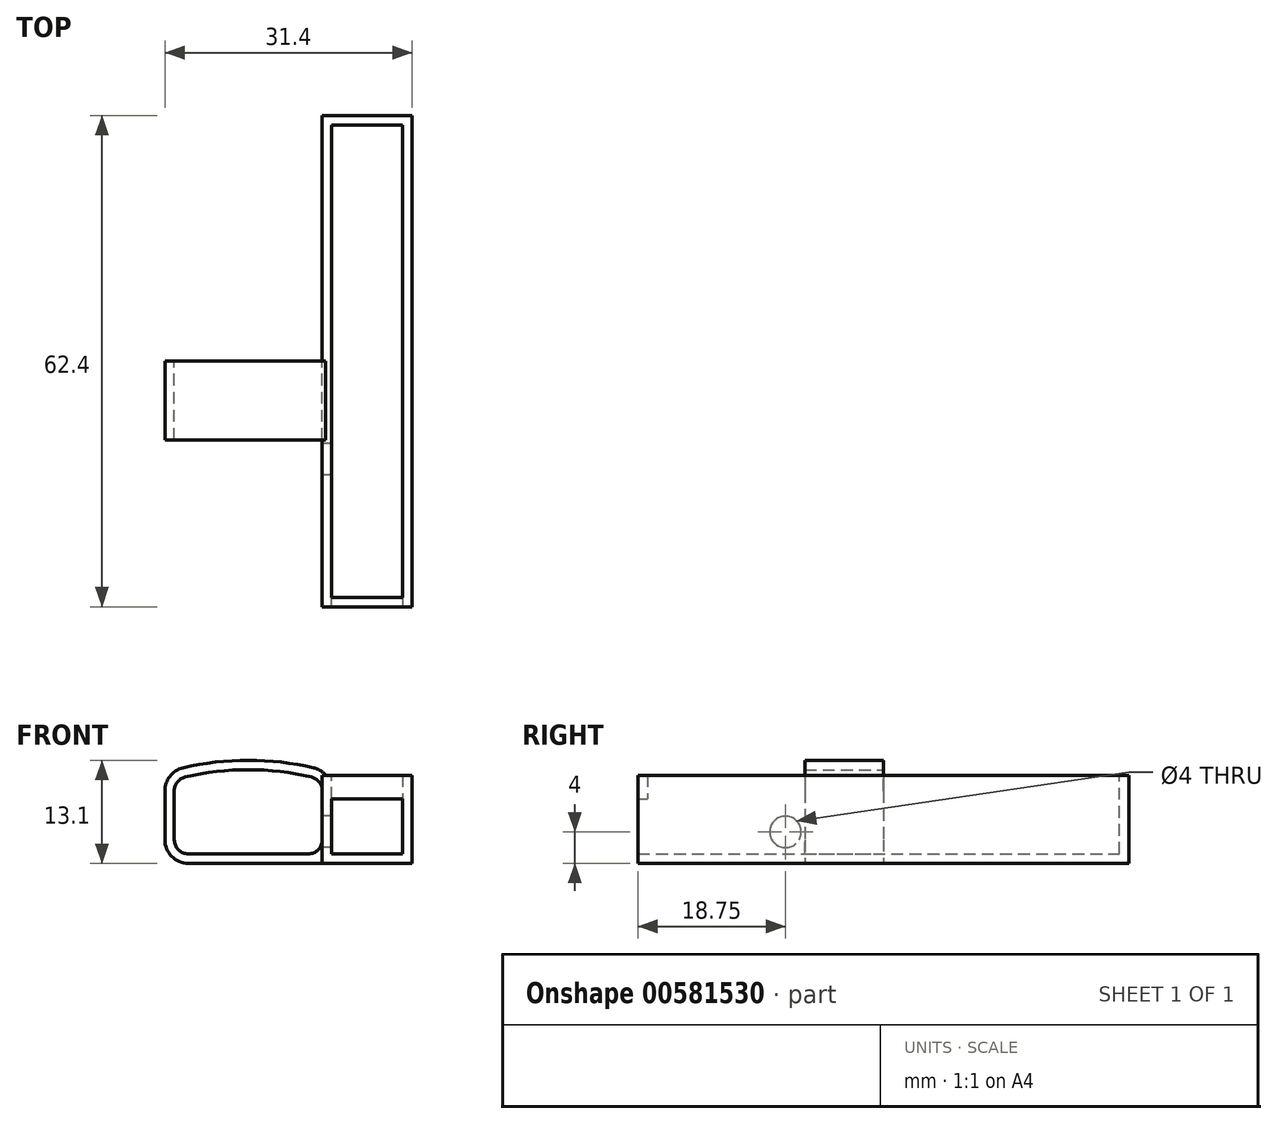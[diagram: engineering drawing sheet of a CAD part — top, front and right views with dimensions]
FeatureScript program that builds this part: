
annotation { "Feature Type Name" : "Feature", "Feature Type Description" : "" }
export const myFeature = defineFeature(function(context is Context, id is Id, definition is map)
    precondition{}
    {
        {
            var Q0;
            Q0=qCreatedBy(makeId("Front.planeOp"),FACE);
            var sketch = newSketch(context, id + "F0", { "sketchPlane" : qUnion([Q0])});
            skLineSegment(sketch, "E0.top", {"start": v(-7.6, -4.7) * mm, "end": v(7.6, -4.7) * mm});
            skLineSegment(sketch, "E0.left", {"start": v(-9.4, 3.3) * mm, "end": v(-9.4, -2.9) * mm});
            skLineSegment(sketch, "E0.right", {"start": v(9.4, 3.3) * mm, "end": v(9.4, -2.9) * mm});
            skPoint(sketch, "E0.middle", {"position": v(0, 0) * mm});
            skArc(sketch, "E1", {"start": v(-8.02, 5.06) * mm, "mid": v(0, 6) * mm, "end": v(8.02, 5.06) * mm});
            skPoint(sketch, "E2", {"position": v(0, 6) * mm});
            skPoint(sketch, "E3", {"position": v(0, -4.7) * mm});
            skPoint(sketch, "E4.visualSharp", {"position": v(-9.4, 4.7) * mm});
            skArc(sketch, "E4.filletArc", {"start": v(-8.02, 5.06) * mm, "mid": v(-9.01, 4.42) * mm, "end": v(-9.4, 3.3) * mm});
            skPoint(sketch, "E5.visualSharp", {"position": v(9.4, 4.7) * mm});
            skArc(sketch, "E5.filletArc", {"start": v(9.4, 3.3) * mm, "mid": v(9.01, 4.42) * mm, "end": v(8.02, 5.06) * mm});
            skPoint(sketch, "E6.visualSharp", {"position": v(-9.4, -4.7) * mm});
            skArc(sketch, "E6.filletArc", {"start": v(-9.4, -2.9) * mm, "mid": v(-8.87, -4.17) * mm, "end": v(-7.6, -4.7) * mm});
            skPoint(sketch, "E7.visualSharp", {"position": v(9.4, -4.7) * mm});
            skArc(sketch, "E7.filletArc", {"start": v(7.6, -4.7) * mm, "mid": v(8.87, -4.17) * mm, "end": v(9.4, -2.9) * mm});
            skSolve(sketch);
        }
        {
            var Q0;
            Q0 = qSketchRegion(id + "F0", true);
            extrude(context, id + "F1", {"entities" : qUnion([Q0]), "depth" : 10 * mm, "offsetDistance" : 25 * mm});
        }
        {
            var Q0;
            Q0=makeQuery(id+"F1.opExtrude","CAP_FACE",FACE,{"disambiguationData":[OSD([sQuery(id+"F0.wireOp",EDGE,"E0.top"),sQuery(id+"F0.wireOp",EDGE,"E0.left"),sQuery(id+"F0.wireOp",EDGE,"E0.right"),sQuery(id+"F0.wireOp",EDGE,"E1"),sQuery(id+"F0.wireOp",EDGE,"E4.filletArc"),sQuery(id+"F0.wireOp",EDGE,"E5.filletArc"),sQuery(id+"F0.wireOp",EDGE,"E6.filletArc"),sQuery(id+"F0.wireOp",EDGE,"E7.filletArc")])],"isStart":true});
            var Q1;
            Q1=makeQuery(id+"F1.opExtrude","CAP_FACE",FACE,{"disambiguationData":[OSD([sQuery(id+"F0.wireOp",EDGE,"E0.top"),sQuery(id+"F0.wireOp",EDGE,"E0.left"),sQuery(id+"F0.wireOp",EDGE,"E0.right"),sQuery(id+"F0.wireOp",EDGE,"E1"),sQuery(id+"F0.wireOp",EDGE,"E4.filletArc"),sQuery(id+"F0.wireOp",EDGE,"E5.filletArc"),sQuery(id+"F0.wireOp",EDGE,"E6.filletArc"),sQuery(id+"F0.wireOp",EDGE,"E7.filletArc")])],"isStart":false});
            shell(context, id + "F2", {"entities" : qUnion([Q0, Q1]), "thickness" : 1.2 * mm, "oppositeDirection" : true});
        }
        {
            var Q0;
            Q0=makeQuery(id+"F1.opExtrude","SWEPT_FACE",FACE,{"disambiguationData":[OSD([sQuery(id+"F0.wireOp",EDGE,"E0.top")])]});
            var sketch = newSketch(context, id + "F3", { "sketchPlane" : qUnion([Q0])});
            skLineSegment(sketch, "E8.bottom", {"start": v(7.6, 10) * mm, "end": v(20.8, 10) * mm});
            skLineSegment(sketch, "E8.top", {"start": v(7.6, 0) * mm, "end": v(20.8, 0) * mm});
            skLineSegment(sketch, "E8.left", {"start": v(7.6, 10) * mm, "end": v(7.6, 0) * mm});
            skLineSegment(sketch, "E8.right", {"start": v(20.8, 10) * mm, "end": v(20.8, 0) * mm});
            skSolve(sketch);
        }
        {
            var Q0;
            Q0=makeQuery(id+"F3.imprint","IMPRINT",FACE,{"disambiguationData":[TD([[makeQuery(id+"F3.imprint","IMPRINT",EDGE,{"derivedFrom":sQuery(id+"F3.wireOp",EDGE,"E8.bottom")}),-1.0]])]});
            var Q1;
            Q1=makeQuery(id+"F2.opShell","OFFSET_FACE",FACE,{"disambiguationData":[OSD([sQuery(id+"F0.wireOp",EDGE,"E0.top")])]});
            extrude(context, id + "F4", {"entities" : qUnion([Q0]), "operationType" : NewBodyOperationType.ADD, "endBound" : BoundingType.UP_TO_SURFACE, "oppositeDirection" : true, "depth" : 25 * mm, "endBoundEntityFace" : qUnion([Q1]), "offsetDistance" : 25 * mm});
        }
        {
            var Q0;
            Q0=makeQuery(id+"F4.opExtrude","CAP_FACE",FACE,{"disambiguationData":[OSD([sQuery(id+"F3.wireOp",EDGE,"E8.bottom"),sQuery(id+"F3.wireOp",EDGE,"E8.top"),sQuery(id+"F3.wireOp",EDGE,"E8.left"),sQuery(id+"F3.wireOp",EDGE,"E8.right")])],"isStart":false});
            var sketch = newSketch(context, id + "F5", { "sketchPlane" : qUnion([Q0])});
            skLineSegment(sketch, "E9.bottom", {"start": v(20.8, 0) * mm, "end": v(19.6, 0) * mm});
            skLineSegment(sketch, "E9.top", {"start": v(20.8, -10) * mm, "end": v(19.6, -10) * mm});
            skLineSegment(sketch, "E9.left", {"start": v(20.8, 0) * mm, "end": v(20.8, -10) * mm});
            skLineSegment(sketch, "E9.right", {"start": v(19.6, 0) * mm, "end": v(19.6, -10) * mm});
            skLineSegment(sketch, "E10.bottom", {"start": v(10.6, -10) * mm, "end": v(10, -10) * mm});
            skLineSegment(sketch, "E10.top", {"start": v(10.6, 0) * mm, "end": v(10, 0) * mm});
            skLineSegment(sketch, "E10.left", {"start": v(10.6, -10) * mm, "end": v(10.6, 0) * mm});
            skLineSegment(sketch, "E10.right", {"start": v(10, -10) * mm, "end": v(10, 0) * mm});
            skSolve(sketch);
        }
        {
            var Q0;
            Q0 = qSketchRegion(id + "F5", true);
            extrude(context, id + "F6", {"entities" : qUnion([Q0]), "operationType" : NewBodyOperationType.ADD, "depth" : 10 * mm, "offsetDistance" : 25 * mm});
        }
        {
            var Q0;
            Q0=qCreatedBy(makeId("Front.planeOp"),FACE);
            var sketch = newSketch(context, id + "F7", { "sketchPlane" : qUnion([Q0])});
            skLineSegment(sketch, "E11.bottom", {"start": v(20.8, 5.3) * mm, "end": v(19.6, 5.3) * mm, "construction": true});
            skLineSegment(sketch, "E11.top", {"start": v(20.8, -5.9) * mm, "end": v(19.6, -5.9) * mm, "construction": true});
            skLineSegment(sketch, "E11.left", {"start": v(20.8, 5.3) * mm, "end": v(20.8, -5.9) * mm, "construction": true});
            skLineSegment(sketch, "E11.right", {"start": v(19.6, 5.3) * mm, "end": v(19.6, -5.9) * mm, "construction": true});
            skLineSegment(sketch, "E12.bottom", {"start": v(20.8, -5.9) * mm, "end": v(10.6, -5.9) * mm, "construction": true});
            skLineSegment(sketch, "E12.top", {"start": v(20.8, -4.7) * mm, "end": v(10.6, -4.7) * mm, "construction": true});
            skLineSegment(sketch, "E12.left", {"start": v(20.8, -5.9) * mm, "end": v(20.8, -4.7) * mm, "construction": true});
            skLineSegment(sketch, "E12.right", {"start": v(10.6, -5.9) * mm, "end": v(10.6, -4.7) * mm, "construction": true});
            skLineSegment(sketch, "E13.bottom", {"start": v(10.6, -5.9) * mm, "end": v(9.4, -5.9) * mm, "construction": true});
            skLineSegment(sketch, "E13.top", {"start": v(10.6, 5.3) * mm, "end": v(9.4, 5.3) * mm, "construction": true});
            skLineSegment(sketch, "E13.left", {"start": v(10.6, -5.9) * mm, "end": v(10.6, 5.3) * mm, "construction": true});
            skLineSegment(sketch, "E14", {"start": v(20.8, 5.3) * mm, "end": v(19.6, 5.3) * mm});
            skLineSegment(sketch, "E15", {"start": v(19.6, 5.3) * mm, "end": v(19.6, -4.7) * mm});
            skLineSegment(sketch, "E16", {"start": v(19.6, -4.7) * mm, "end": v(10.6, -4.7) * mm});
            skLineSegment(sketch, "E17", {"start": v(10.6, 5.3) * mm, "end": v(9.4, 5.3) * mm});
            skLineSegment(sketch, "E18", {"start": v(9.4, -5.9) * mm, "end": v(20.8, -5.9) * mm});
            skLineSegment(sketch, "E19", {"start": v(20.8, 5.3) * mm, "end": v(20.8, -5.9) * mm});
            skLineSegment(sketch, "E20", {"start": v(10.6, 5.3) * mm, "end": v(10.6, -4.7) * mm});
            skLineSegment(sketch, "E21", {"start": v(9.4, -5.9) * mm, "end": v(9.4, 5.3) * mm});
            skSolve(sketch);
        }
        {
            var Q0;
            Q0 = qSketchRegion(id + "F7", true);
            extrude(context, id + "F8", {"entities" : qUnion([Q0]), "operationType" : NewBodyOperationType.ADD, "depth" : 31.2 * mm, "offsetDistance" : 25 * mm, "hasSecondDirection" : true, "secondDirectionOppositeDirection" : true, "secondDirectionDepth" : 31.2 * mm});
        }
        {
            var Q0;
            Q0=makeQuery(id+"F8.boolean.opBoolean","MERGE",FACE,{"derivedFrom":[makeQuery(id+"F2.opShell","OFFSET_FACE",FACE,{"disambiguationData":[OSD([sQuery(id+"F0.wireOp",EDGE,"E0.right")])]}),makeQuery(id+"F8.opExtrude","SWEPT_FACE",FACE,{"disambiguationData":[OSD([sQuery(id+"F7.wireOp",EDGE,"E21")])]})]});
            var sketch = newSketch(context, id + "F9", { "sketchPlane" : qUnion([Q0])});
            skPoint(sketch, "E22", {"position": v(12.45, -1.9) * mm});
            skSolve(sketch);
        }
        {
            var Q0;
            Q0=sQuery(id+"F9.wireOp",VERTEX,"E22");
            var Q1;
            Q1=makeQuery(id+"F1.opExtrude","SWEPT_BODY",BODY,{"disambiguationData":[OSD([sQuery(id+"F0.wireOp",EDGE,"E0.top"),sQuery(id+"F0.wireOp",EDGE,"E0.left"),sQuery(id+"F0.wireOp",EDGE,"E0.right"),sQuery(id+"F0.wireOp",EDGE,"E1"),sQuery(id+"F0.wireOp",EDGE,"E4.filletArc"),sQuery(id+"F0.wireOp",EDGE,"E5.filletArc"),sQuery(id+"F0.wireOp",EDGE,"E6.filletArc"),sQuery(id+"F0.wireOp",EDGE,"E7.filletArc")])]});
            hole(context, id + "F10", {"style" : HoleStyle.SIMPLE, "endStyle" : HoleEndStyle.BLIND, "holeDiameter" : 4 * mm, "majorDiameter" : 5 * mm, "holeDepth" : 5 * mm, "isTappedThrough" : true, "tappedDepth" : 12 * mm, "tapClearance" : 3, "locations" : qUnion([Q0]), "scope" : qUnion([Q1])});
        }
        {
            var Q0;
            Q0=makeQuery(id+"F8.opExtrude","CAP_FACE",FACE,{"disambiguationData":[OSD([sQuery(id+"F7.wireOp",EDGE,"E14"),sQuery(id+"F7.wireOp",EDGE,"E15"),sQuery(id+"F7.wireOp",EDGE,"E16"),sQuery(id+"F7.wireOp",EDGE,"E17"),sQuery(id+"F7.wireOp",EDGE,"E18"),sQuery(id+"F7.wireOp",EDGE,"E19"),sQuery(id+"F7.wireOp",EDGE,"E20"),sQuery(id+"F7.wireOp",EDGE,"E21")])],"isStart":true});
            var sketch = newSketch(context, id + "F11", { "sketchPlane" : qUnion([Q0])});
            skLineSegment(sketch, "E23.bottom", {"start": v(-20.8, -5.9) * mm, "end": v(-9.4, -5.9) * mm});
            skLineSegment(sketch, "E23.top", {"start": v(-20.8, 5.3) * mm, "end": v(-9.4, 5.3) * mm});
            skLineSegment(sketch, "E23.left", {"start": v(-20.8, -5.9) * mm, "end": v(-20.8, 5.3) * mm});
            skLineSegment(sketch, "E23.right", {"start": v(-9.4, -5.9) * mm, "end": v(-9.4, 5.3) * mm});
            skSolve(sketch);
        }
        {
            var Q0;
            Q0 = qSketchRegion(id + "F11", true);
            extrude(context, id + "F12", {"entities" : qUnion([Q0]), "operationType" : NewBodyOperationType.ADD, "oppositeDirection" : true, "depth" : 1.2 * mm, "offsetDistance" : 25 * mm});
        }
        {
            var Q0;
            Q0=makeQuery(id+"F8.opExtrude","CAP_FACE",FACE,{"disambiguationData":[OSD([sQuery(id+"F7.wireOp",EDGE,"E14"),sQuery(id+"F7.wireOp",EDGE,"E15"),sQuery(id+"F7.wireOp",EDGE,"E16"),sQuery(id+"F7.wireOp",EDGE,"E17"),sQuery(id+"F7.wireOp",EDGE,"E18"),sQuery(id+"F7.wireOp",EDGE,"E19"),sQuery(id+"F7.wireOp",EDGE,"E20"),sQuery(id+"F7.wireOp",EDGE,"E21")])],"isStart":false});
            var sketch = newSketch(context, id + "F13", { "sketchPlane" : qUnion([Q0])});
            skLineSegment(sketch, "E24.bottom", {"start": v(9.4, 5.3) * mm, "end": v(20.8, 5.3) * mm});
            skLineSegment(sketch, "E24.top", {"start": v(9.4, 2.3) * mm, "end": v(20.8, 2.3) * mm});
            skLineSegment(sketch, "E24.left", {"start": v(9.4, 5.3) * mm, "end": v(9.4, 2.3) * mm});
            skLineSegment(sketch, "E24.right", {"start": v(20.8, 5.3) * mm, "end": v(20.8, 2.3) * mm});
            skSolve(sketch);
        }
        {
            var Q0;
            Q0 = qSketchRegion(id + "F13", true);
            extrude(context, id + "F14", {"entities" : qUnion([Q0]), "operationType" : NewBodyOperationType.ADD, "oppositeDirection" : true, "depth" : 1.2 * mm, "offsetDistance" : 25 * mm});
        }
    });
